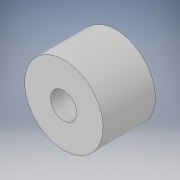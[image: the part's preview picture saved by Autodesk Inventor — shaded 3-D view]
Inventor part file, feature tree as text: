
AUTODESK INVENTOR PART (.ipt)
format: ipt  version: 2019 (Build 230136000, 136)  size: 99,840 bytes
history: native  units: in
note: dims shown in document units (in); Inventor stores cm internally (conversion verified against a paired STEP export)
features: sketch x2, extrude x1, hole x1
ambient origin geometry x8: Origin, YZ Plane, XZ Plane, XY Plane, X Axis, Y Axis, Z Axis, Center Point
bodies: Solid1 (feature_tree)
feature tree (4):
  extrude  "Extrusion1"  Depth=0.375in
  hole  "Hole1"  [1 undecoded]
  sketch  "Sketch1"  dims[d1=0.5in d2=0.0in]
  sketch  "Sketch2"  dims[d3=0.25in d4=0.75in d5=0.375in d6=0.25in d7=0.5635in d8=1.0in d9=0.8108in d10=0.75in d11=0.8108in d12=0.0625in d13=0.75in d14=0.375in]
note: 1 required parameter value undecoded (feature->parameter linkage not recoverable at this tier; creation-order binding heuristic only, values carry confidence <= 0.55)
